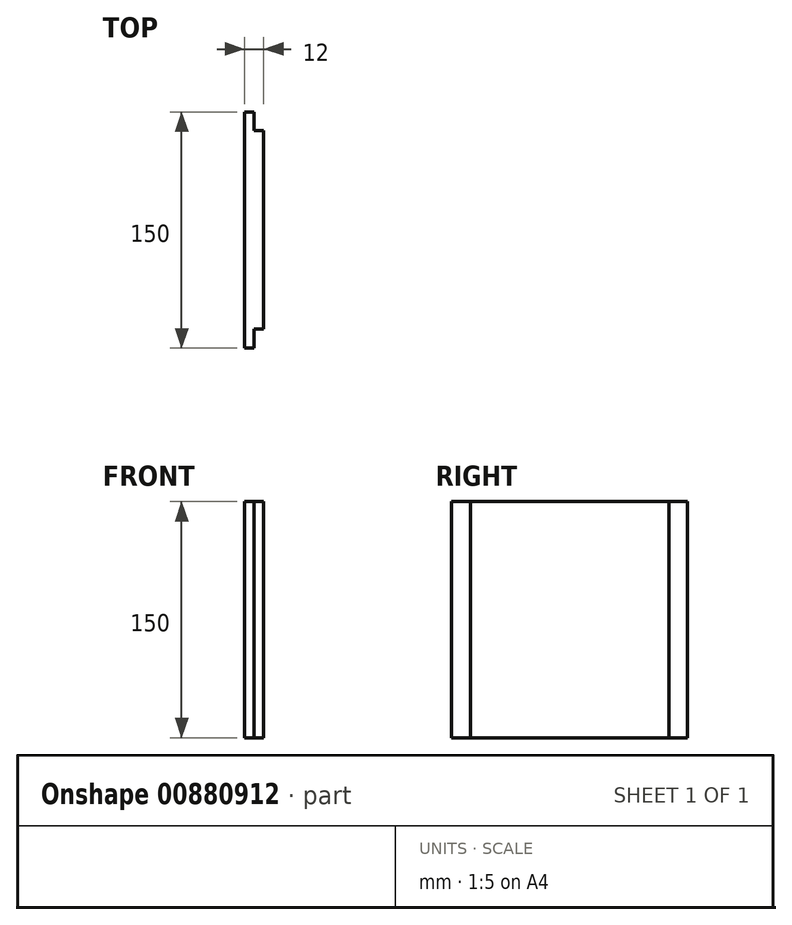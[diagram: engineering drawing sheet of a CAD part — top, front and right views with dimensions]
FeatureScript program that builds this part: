
annotation { "Feature Type Name" : "Feature", "Feature Type Description" : "" }
export const myFeature = defineFeature(function(context is Context, id is Id, definition is map)
    precondition{}
    {
        {
            var Q0;
            Q0=qCreatedBy(makeId("Top.planeOp"),FACE);
            var sketch = newSketch(context, id + "F0", { "sketchPlane" : qUnion([Q0])});
            skLineSegment(sketch, "E0.bottom", {"start": v(0, -75) * mm, "end": v(-6, -75) * mm});
            skLineSegment(sketch, "E0.top", {"start": v(0, 75) * mm, "end": v(-6, 75) * mm});
            skLineSegment(sketch, "E0.left", {"start": v(6, -63) * mm, "end": v(6, 63) * mm});
            skLineSegment(sketch, "E0.right", {"start": v(-6, -75) * mm, "end": v(-6, 75) * mm});
            skPoint(sketch, "E0.middle", {"position": v(0, 0) * mm});
            skLineSegment(sketch, "E1", {"start": v(0, 75) * mm, "end": v(0, 63) * mm});
            skLineSegment(sketch, "E2", {"start": v(0, 63) * mm, "end": v(6, 63) * mm});
            skLineSegment(sketch, "E3", {"start": v(0, -75) * mm, "end": v(0, -63) * mm});
            skLineSegment(sketch, "E4", {"start": v(6, -63) * mm, "end": v(0, -63) * mm});
            skPoint(sketch, "E5.orphan", {"position": v(6, -75) * mm});
            skPoint(sketch, "E6.orphan", {"position": v(6, 75) * mm});
            skSolve(sketch);
        }
        {
            var Q0;
            Q0=makeQuery(id+"F0.imprint","IMPRINT",FACE,{"disambiguationData":[TD([[makeQuery(id+"F0.imprint","IMPRINT",EDGE,{"derivedFrom":sQuery(id+"F0.wireOp",EDGE,"E0.bottom")}),-1.0]])]});
            extrude(context, id + "F1", {"entities" : qUnion([Q0]), "depth" : 150 * mm, "offsetDistance" : 25 * mm});
        }
    });
